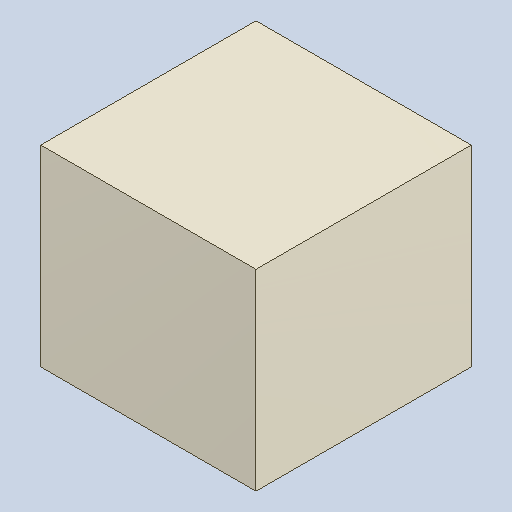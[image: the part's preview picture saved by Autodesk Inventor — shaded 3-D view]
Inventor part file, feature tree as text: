
AUTODESK INVENTOR PART (.ipt)
format: ipt  version: 2023.4 (Build 274418000, 418)  size: 81,920 bytes
history: native  units: mm
features: extrude x1
ambient origin geometry x8: Origin, YZ Plane, XZ Plane, XY Plane, X Axis, Y Axis, Z Axis, Center Point
bodies: Solid1 (feature_tree)
feature tree (1):
  extrude  "Extruded_3"  [1 undecoded]
note: 1 required parameter value undecoded (feature->parameter linkage not recoverable at this tier; creation-order binding heuristic only, values carry confidence <= 0.55)
